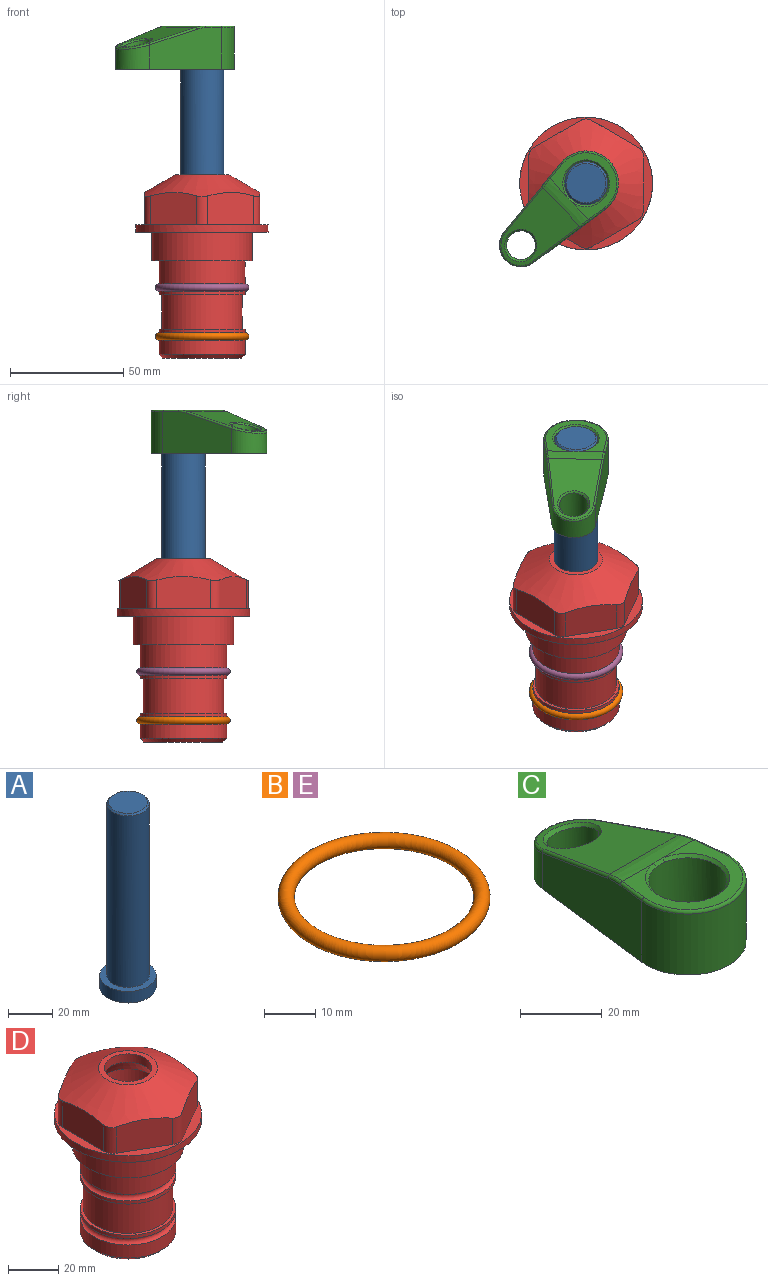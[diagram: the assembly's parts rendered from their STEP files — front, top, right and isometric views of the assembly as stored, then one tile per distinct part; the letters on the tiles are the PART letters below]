
ASSEMBLY  parts=5 mates=4
PART A: 6 faces, bbox 25.4x25.4x101.6 mm
  f0: plane 17.46x17.46mm, normal (0,0,1), area 239.5mm2, adj f5
  f1: plane 25.4x25.4mm, normal (0,0,-1), area 506.7mm2, adj f2
  f2: cylinder r=12.7mm len=25.4mm, axis (0,0,1), area 506.7mm2, adj f1,f3
  f3: plane 25.4x25.4mm, normal (0,0,1), area 221.7mm2, adj f2,f4
  f4: cylinder r=9.53mm len=94.46mm, axis (0,0,1), area 5653mm2, adj f3,f5
  f5: cone r=8.73mm half-angle=45deg, axis (0,0,-1), area 64.4mm2, adj f0,f4
PART B: 1 faces, bbox 44.7x44.7x3.2 mm
  f0: torus R=19.05mm, axis (0,0,1), area 1193.9mm2
PART C: 31 faces, bbox 31.7x65.5x19.8 mm
  f0: plane 39.12x18.26mm, normal (0.99,0.12,0), area 612.2mm2, adj f1,f4,f7,f11,f13,f15
  f1: cylinder r=9.53mm len=18.91mm, axis (0,0,-1), area 296.1mm2, adj f0,f2,f7,f17
  f2: plane 39.12x18.26mm, normal (-0.99,0.12,0), area 612.2mm2, adj f1,f4,f7,f12,f14,f16
  f3: cylinder r=6.35mm len=12.7mm, axis (0,0,-1), area 362.4mm2, adj f7,f18
  f4: cylinder r=14.29mm len=28.58mm, axis (0,0,-1), area 882.2mm2, adj f0,f2,f7,f10
  f5: cylinder r=9.53mm len=19.05mm, axis (0,0,-1), area 1092.6mm2, adj f7,f19,f20
  f6: plane 26.99x23.69mm, normal (0,0,1), area 216.2mm2, adj f9,f10,f11,f12,f19
  f7: plane 63.5x28.58mm, normal (0,0,-1), area 661.8mm2, adj f0,f1,f2,f3,f4,f5,f22,f23
  f8: plane 33.52x23.6mm, normal (0,0.26,0.97), area 486mm2, adj f9,f15,f16,f17,f18
  f9: cylinder r=19.05mm len=24.72mm, axis (1,0,0), area 120.4mm2, adj f6,f8,f13,f14,f20
  f10: torus R=13.49mm, axis (0,0,1), area 59mm2, adj f4,f6,f11,f12
  f11: cylinder r=0.79mm len=8.67mm, axis (0.12,-0.99,0), area 10.8mm2, adj f0,f6,f10,f13
  f12: cylinder r=0.79mm len=8.67mm, axis (0.12,0.99,0), area 10.8mm2, adj f2,f6,f10,f14
  f13: bspline ~4.95x1.42mm, area 6.1mm2, adj f0,f9,f11,f15
  f14: bspline ~4.95x1.42mm, area 6.1mm2, adj f2,f9,f12,f16
  f15: cylinder r=0.79mm len=25.95mm, axis (0.12,-0.96,0.26), area 32.9mm2, adj f0,f8,f13,f17
  f16: cylinder r=0.79mm len=25.95mm, axis (0.12,0.96,-0.26), area 32.9mm2, adj f2,f8,f14,f17
  f17: bspline ~18.91x8.38mm, area 30mm2, adj f1,f8,f15,f16
  f18: bspline ~14.29x14.29mm, area 48.3mm2, adj f3,f8
  f19: cone r=9.53mm half-angle=45deg, axis (0,0,1), area 66.5mm2, adj f5,f6,f20
  f20: bspline ~3.22x0.96mm, area 3.5mm2, adj f5,f9,f19
  f21: plane 2.75x2.72mm, normal (0,0,-1), area 2.9mm2, adj f23,f25,f28
  f22: plane 23.05x15.88mm, normal (-0.99,-0.12,0), area 323.6mm2, adj f7,f25,f26,f27,f28,f29
  f23: plane 23.05x15.88mm, normal (0.99,-0.12,0), area 323.6mm2, adj f7,f21,f25,f27,f28,f30
  f24: cylinder r=9.53mm len=10.69mm, axis (0,0,-1), area 114.7mm2, adj f7,f27,f29,f30
  f25: cylinder r=12.7mm len=20.59mm, axis (0,0,-1), area 381.1mm2, adj f7,f21,f22,f23,f26,f28
  f26: plane 2.75x2.72mm, normal (0,0,-1), area 2.9mm2, adj f22,f25,f28
  f27: plane 19.72x18.37mm, normal (0,-0.26,-0.97), area 291.8mm2, adj f22,f23,f24,f28,f29,f30
  f28: cylinder r=15.88mm len=19.92mm, axis (1,0,0), area 54.8mm2, adj f21,f22,f23,f25,f26,f27
  f29: cylinder r=1.59mm len=11mm, axis (0,0,-1), area 34.7mm2, adj f7,f22,f24,f27
  f30: cylinder r=1.59mm len=11mm, axis (0,0,-1), area 34.7mm2, adj f7,f23,f24,f27
PART D: 36 faces, bbox 58.7x58.7x81 mm
  f0: cylinder r=17.78mm len=35.56mm, axis (0,0,1), area 1670.8mm2, adj f23,f24,f31
  f1: cylinder r=19.05mm len=38.1mm, axis (0,0,1), area 1191.9mm2, adj f26,f27,f30
  f2: plane 58.66x58.66mm, normal (0,0,-1), area 1150.6mm2, adj f3,f28
  f3: cylinder r=29.33mm len=58.66mm, axis (0,0,-1), area 585.1mm2, adj f2,f4
  f4: plane 58.66x58.66mm, normal (0,0,1), area 475.9mm2, adj f3,f5,f6,f7,f8,f9,f10,f11
  f5: plane 20.32x14.34mm, normal (-0.5,0.87,0), area 324.4mm2, adj f4,f15,f16,f17
  f6: plane 20.32x14.34mm, normal (0.5,0.87,0), area 324.4mm2, adj f4,f14,f15,f17
  f7: plane 23.48x14.34mm, normal (1,0,0), area 324.4mm2, adj f4,f13,f14,f17
  f8: plane 20.32x14.34mm, normal (0.5,-0.87,0), area 324.4mm2, adj f4,f12,f13,f17
  f9: plane 20.32x14.34mm, normal (-0.5,-0.87,0), area 324.4mm2, adj f4,f11,f12,f17
  f10: plane 23.48x14.34mm, normal (-1,0,0), area 324.4mm2, adj f4,f11,f16,f17
  f11: cylinder r=5.08mm len=12.85mm, axis (0,0,-1), area 67.2mm2, adj f4,f9,f10,f17
  f12: cylinder r=5.08mm len=12.85mm, axis (0,0,-1), area 67.2mm2, adj f4,f8,f9,f17
  f13: cylinder r=5.08mm len=12.85mm, axis (0,0,-1), area 67.2mm2, adj f4,f7,f8,f17
  f14: cylinder r=5.08mm len=12.85mm, axis (0,0,-1), area 67.2mm2, adj f4,f6,f7,f17
  f15: cylinder r=5.08mm len=12.85mm, axis (0,0,-1), area 67.2mm2, adj f4,f5,f6,f17
  f16: cylinder r=5.08mm len=12.85mm, axis (0,0,-1), area 67.2mm2, adj f4,f5,f10,f17
  f17: cone r=11.73mm half-angle=60deg, axis (0,0,-1), area 2071.8mm2, adj f5,f6,f7,f8,f9,f10,f11,f12
  f18: plane 23.46x23.46mm, normal (0,0,1), area 147.4mm2, adj f17,f35
  f19: plane 34.93x34.93mm, normal (0,0,-1), area 958mm2, adj f29
  f20: cylinder r=19.05mm len=38.1mm, axis (0,0,1), area 760.1mm2, adj f21,f29
  f21: torus R=19.05mm, axis (0,0,1), area 565.3mm2, adj f20,f22
  f22: cylinder r=19.05mm len=38.1mm, axis (0,0,1), area 190mm2, adj f21,f23
  f23: plane 38.1x38.1mm, normal (0,0,1), area 146.9mm2, adj f0,f22
  f24: plane 38.1x38.1mm, normal (0,0,-1), area 146.9mm2, adj f0,f25
  f25: cylinder r=19.05mm len=38.1mm, axis (0,0,1), area 190mm2, adj f24,f26
  f26: torus R=19.05mm, axis (0,0,1), area 565.3mm2, adj f1,f25
  f27: plane 44.45x44.45mm, normal (0,0,-1), area 411.7mm2, adj f1,f28
  f28: cylinder r=22.23mm len=44.45mm, axis (0,0,1), area 1773.5mm2, adj f2,f27
  f29: cone r=19.05mm half-angle=45deg, axis (0,0,1), area 257.5mm2, adj f19,f20
  f30: cylinder r=3.17mm len=6.75mm, axis (-1,0,0), area 128mm2, adj f1,f33
  f31: cylinder r=3.17mm len=6.35mm, axis (-1,0,0), area 102.5mm2, adj f0,f33
  f32: plane 25.4x25.4mm, normal (0,0,1), area 506.7mm2, adj f33
  f33: cylinder r=12.7mm len=66.42mm, axis (0,0,-1), area 5236.2mm2, adj f30,f31,f32,f34
  f34: cone r=9.53mm half-angle=30deg, axis (0,0,-1), area 443.4mm2, adj f33,f35
  f35: cylinder r=9.53mm len=19.05mm, axis (0,0,-1), area 240.9mm2, adj f18,f34
PART E: same geometry as B
PLACE A rot(axis=(0,0,1),133.6deg) t=(0,0,27.55)mm
PLACE B t=(0,0,-21.59)mm
PLACE C rot(axis=(0,0,1),133.6deg) t=(0,0,27.55)mm
PLACE D at identity fixed
PLACE E at identity
MATE fastened E.f0 <-> D.f0  axis (0,0,1) through (0,0,-24.51)mm
MATE cylindrical A.f2 <-> D.f0  axis (0,0,-1) through (0,0,-10.55)mm
MATE fastened B.f0 <-> D.f0  axis (0,0,1) through (0,0,-46.1)mm
MATE fastened A.f2 <-> C.f4  axis (0,0,1) through (0,0,91.05)mm
